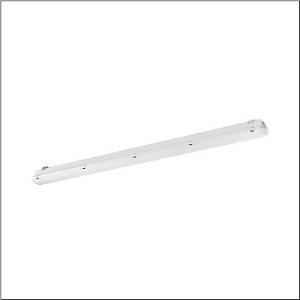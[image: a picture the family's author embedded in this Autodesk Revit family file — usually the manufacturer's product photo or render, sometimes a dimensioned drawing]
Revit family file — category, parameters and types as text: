
# Revit family: monsun_r__11xtreme_mo_51fe10dp460j_08a3
name_source: partatom
category: Lighting Fixtures
units: mm (PartAtom-declared; Revit-internal decimal feet)

## family parameters
Cut with Voids When Loaded = No
Host = Face
Light Source = No
Part Type = Normal
Room Calculation Point = No
Round Connector Dimension = Use Diameter
Shared = No

## types (1)
- --- (1 x LED, 6370 lm, 36.5 W, 4000K)
    Apparent Load = 37 VA
    CIE Flux Codes = 47 77 93 94 100
    Color Rendering = 80
    Color Temperature = 4000K
    Default Elevation = 1800 mm
    Description = Monsun® 11Xtreme MO, damp-proof luminaire, chain hanger, primary optical cover: enclosure, of PMMA, light emission: direct distribution, primary light characteristic: symmetric, installation type: suspended mounting, surface-mounted, horizontal mounting, vertical mounting, LED, rated luminous flux: 6.370lm, luminous efficacy: 175lm/W, light colour: 840, colour temperature: 4000K, control gear: ECG DALI, with terminal, 5-pole, max. 2.5mm², mains connection: 220..240V, AC, 50/60Hz, rated input power: 37W, luminaire housing, of glass-fibre reinforced polyester, uncoated, bright grey, length: 1.590mm, width: 90mm, height: 88mm, clip for enclosure, of stainless steel (V2A), ceiling mounting element, of stainless steel (V2A), chain hanger, of stainless steel (V2A), protection rating (complete): IP66, insulation class (complete): insulation class I (protective earthing), certification: CE, ENEC, VDE, UKCA, protection symbol: D, impact resistance: IK04, permissible operating ambient temperature: -35..+55°C, standard: EN 60598-2-1, EN 50419, corresponds to IFS (International Featured Standards) requirements for safety and quality in the food industry, for indoor or canopied outdoor use, no direct snow, no direct sun, no direct rain, packaging unit: 1 piece
    Height = 88 mm
    Lamp = 1 x LED
    Lamp Light Flux = 6370 lm
    Lamp Power = 36.5 W
    Lamp count = 1
    Length = 1590 mm
    Luminous efficacy = 175 lm/W
    Manufacturer = Siteco
    ModVariant = No
    Model = 51FE10DP460J
    Mounting Place = Ceiling
    Mounting Type = Pendant
    Number of Poles = 1
    OnlyDefault = Yes
    Power Factor = 1
    Product Name = Monsun® 11Xtreme MO
    Product group = damp-proof luminaire | ceiling pendant
    ProductGroupID = 908
    Protection Class = Protection class I
    Protection Degree = IP 66
    RLX_Detail_Level = 1
    RlxData = <blob elided: 87065 chars, md5=3a040062>
    Socket = socket
    Standby Power = 0 W
    System Light Flux = 6370 lm
    System Power = 37 W
    Type Comments = factory setting: luminous flux: 100 % | dim-lin: 254 | 240 mA
    Type Image = l_1006851.jpg
    URL = http://relux.com
    VarID = @adj_121437
    Voltage = 0 V
    Weight = 0.00 kg
    Width = 90 mm

## geometry (parser evidence)
native form markers: Blend x4, Sweep x12
no freeform markers — native parametric forms only
